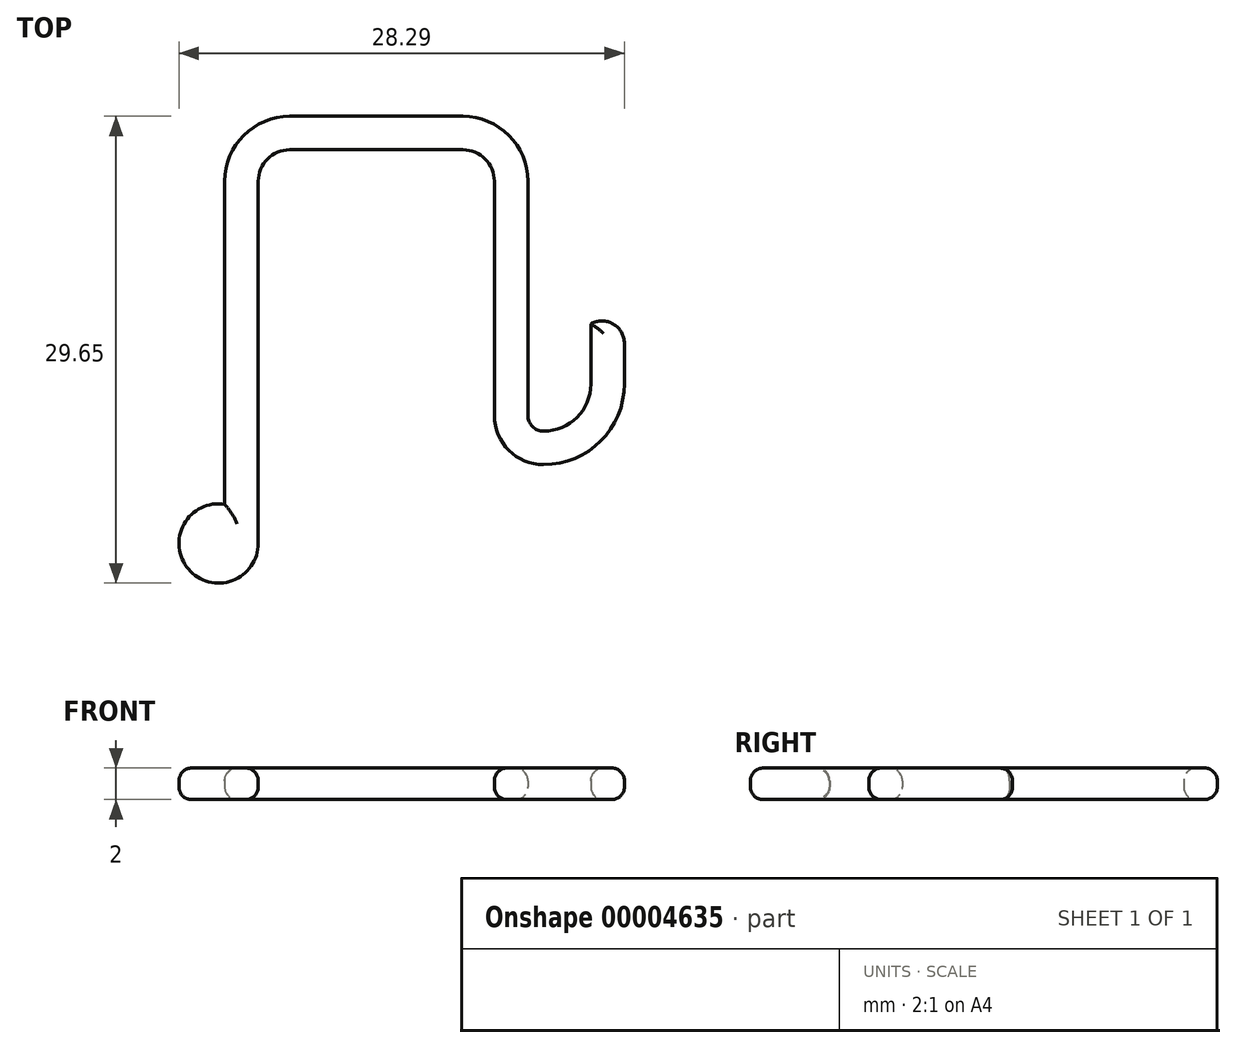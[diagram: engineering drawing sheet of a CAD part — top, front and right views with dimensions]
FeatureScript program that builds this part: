
annotation { "Feature Type Name" : "Feature", "Feature Type Description" : "" }
export const myFeature = defineFeature(function(context is Context, id is Id, definition is map)
    precondition{}
    {
        {
            var Q0;
            Q0=qCreatedBy(makeId("Top.planeOp"),FACE);
            var sketch = newSketch(context, id + "F0", { "sketchPlane" : qUnion([Q0])});
            skLineSegment(sketch, "E0", {"start": v(0, -4.13) * mm, "end": v(0, -19) * mm});
            skLineSegment(sketch, "E1", {"start": v(1, -20) * mm, "end": v(1, -20) * mm});
            skLineSegment(sketch, "E2", {"start": v(4, -17) * mm, "end": v(4, -13.19) * mm});
            skLineSegment(sketch, "E3", {"start": v(6.13, -14.42) * mm, "end": v(6.13, -17) * mm});
            skLineSegment(sketch, "E4", {"start": v(1, -22.13) * mm, "end": v(1, -22.13) * mm});
            skLineSegment(sketch, "E5", {"start": v(-2.13, -19) * mm, "end": v(-2.13, -4.13) * mm});
            skLineSegment(sketch, "E6", {"start": v(-4.13, -2.13) * mm, "end": v(-15.13, -2.13) * mm});
            skLineSegment(sketch, "E7", {"start": v(-17.13, -4.13) * mm, "end": v(-17.13, -27.13) * mm});
            skLineSegment(sketch, "E8", {"start": v(-19.26, -24.64) * mm, "end": v(-19.26, -4.13) * mm});
            skLineSegment(sketch, "E9", {"start": v(-15.13, 0) * mm, "end": v(-4.13, 0) * mm});
            skPoint(sketch, "E10.visualSharp", {"position": v(-17.13, -2.13) * mm});
            skArc(sketch, "E10.filletArc", {"start": v(-15.13, -2.13) * mm, "mid": v(-16.54, -2.71) * mm, "end": v(-17.13, -4.13) * mm});
            skPoint(sketch, "E11.visualSharp", {"position": v(-2.13, -2.13) * mm});
            skArc(sketch, "E11.filletArc", {"start": v(-2.13, -4.13) * mm, "mid": v(-2.71, -2.71) * mm, "end": v(-4.13, -2.13) * mm});
            skPoint(sketch, "E12.visualSharp", {"position": v(0, -20) * mm});
            skArc(sketch, "E12.filletArc", {"start": v(0, -19) * mm, "mid": v(0.3, -19.7) * mm, "end": v(1, -20) * mm});
            skPoint(sketch, "E13.visualSharp", {"position": v(4, -20) * mm});
            skArc(sketch, "E13.filletArc", {"start": v(1, -20) * mm, "mid": v(3.12, -19.12) * mm, "end": v(4, -17) * mm});
            skPoint(sketch, "E14.visualSharp", {"position": v(-2.13, -22.13) * mm});
            skArc(sketch, "E14.filletArc", {"start": v(-2.13, -19) * mm, "mid": v(-1.21, -21.21) * mm, "end": v(1, -22.13) * mm});
            skPoint(sketch, "E15.visualSharp", {"position": v(6.13, -22.13) * mm});
            skArc(sketch, "E15.filletArc", {"start": v(1, -22.13) * mm, "mid": v(4.63, -20.63) * mm, "end": v(6.13, -17) * mm});
            skPoint(sketch, "E16.visualSharp", {"position": v(-19.26, 0) * mm});
            skArc(sketch, "E16.filletArc", {"start": v(-15.13, 0) * mm, "mid": v(-18.05, -1.2) * mm, "end": v(-19.26, -4.13) * mm});
            skPoint(sketch, "E17.visualSharp", {"position": v(0, 0) * mm});
            skArc(sketch, "E17.filletArc", {"start": v(0, -4.13) * mm, "mid": v(-1.2, -1.2) * mm, "end": v(-4.13, 0) * mm});
            skArc(sketch, "E18", {"start": v(6.13, -14.42) * mm, "mid": v(5.42, -13.2) * mm, "end": v(4, -13.19) * mm});
            skArc(sketch, "E19", {"start": v(-17.13, -27.13) * mm, "mid": v(-21.56, -28.76) * mm, "end": v(-19.26, -24.64) * mm});
            skSolve(sketch);
        }
        {
            var Q0;
            Q0=makeQuery(id+"F0.imprint","IMPRINT",FACE,{"disambiguationData":[TD([[makeQuery(id+"F0.imprint","IMPRINT",EDGE,{"derivedFrom":sQuery(id+"F0.wireOp",EDGE,"E0")}),-1.0]])]});
            extrude(context, id + "F1", {"entities" : qUnion([Q0]), "depth" : 2 * mm});
        }
        {
            var Q0;
            Q0=makeQuery(id+"F1.opExtrude","CAP_FACE",FACE,{"disambiguationData":[OSD([sQuery(id+"F0.wireOp",EDGE,"E0"),sQuery(id+"F0.wireOp",EDGE,"E1"),sQuery(id+"F0.wireOp",EDGE,"E2"),sQuery(id+"F0.wireOp",EDGE,"E3"),sQuery(id+"F0.wireOp",EDGE,"E4"),sQuery(id+"F0.wireOp",EDGE,"E5"),sQuery(id+"F0.wireOp",EDGE,"E6"),sQuery(id+"F0.wireOp",EDGE,"E7"),sQuery(id+"F0.wireOp",EDGE,"E8"),sQuery(id+"F0.wireOp",EDGE,"E9"),sQuery(id+"F0.wireOp",EDGE,"E10.filletArc"),sQuery(id+"F0.wireOp",EDGE,"E11.filletArc"),sQuery(id+"F0.wireOp",EDGE,"E12.filletArc"),sQuery(id+"F0.wireOp",EDGE,"E13.filletArc"),sQuery(id+"F0.wireOp",EDGE,"E14.filletArc"),sQuery(id+"F0.wireOp",EDGE,"E15.filletArc"),sQuery(id+"F0.wireOp",EDGE,"E16.filletArc"),sQuery(id+"F0.wireOp",EDGE,"E17.filletArc"),sQuery(id+"F0.wireOp",EDGE,"E18"),sQuery(id+"F0.wireOp",EDGE,"E19")])],"isStart":false});
            var Q1;
            Q1=makeQuery(id+"F1.opExtrude","CAP_FACE",FACE,{"disambiguationData":[OSD([sQuery(id+"F0.wireOp",EDGE,"E0"),sQuery(id+"F0.wireOp",EDGE,"E1"),sQuery(id+"F0.wireOp",EDGE,"E2"),sQuery(id+"F0.wireOp",EDGE,"E3"),sQuery(id+"F0.wireOp",EDGE,"E4"),sQuery(id+"F0.wireOp",EDGE,"E5"),sQuery(id+"F0.wireOp",EDGE,"E6"),sQuery(id+"F0.wireOp",EDGE,"E7"),sQuery(id+"F0.wireOp",EDGE,"E8"),sQuery(id+"F0.wireOp",EDGE,"E9"),sQuery(id+"F0.wireOp",EDGE,"E10.filletArc"),sQuery(id+"F0.wireOp",EDGE,"E11.filletArc"),sQuery(id+"F0.wireOp",EDGE,"E12.filletArc"),sQuery(id+"F0.wireOp",EDGE,"E13.filletArc"),sQuery(id+"F0.wireOp",EDGE,"E14.filletArc"),sQuery(id+"F0.wireOp",EDGE,"E15.filletArc"),sQuery(id+"F0.wireOp",EDGE,"E16.filletArc"),sQuery(id+"F0.wireOp",EDGE,"E17.filletArc"),sQuery(id+"F0.wireOp",EDGE,"E18"),sQuery(id+"F0.wireOp",EDGE,"E19")])],"isStart":true});
            fillet(context, id + "F2", {"entities" : qUnion([Q0, Q1]), "radius" : 0.8 * mm, "tangentPropagation" : true, "allowEdgeOverflow" : false});
        }
    });
